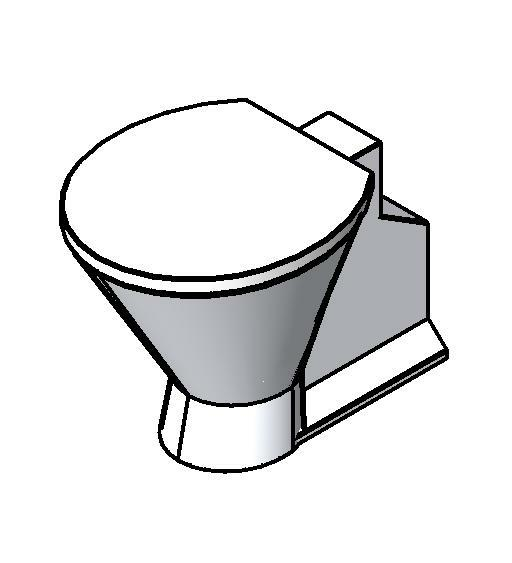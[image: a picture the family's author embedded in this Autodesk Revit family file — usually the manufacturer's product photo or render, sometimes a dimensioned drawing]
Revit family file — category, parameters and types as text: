
# Revit family: 23799-Deca_Torneira de Parede Cromado_Gama_1178-13
name_source: partatom
category: Plumbing Fixtures
units: mm (PartAtom-declared; Revit-internal decimal feet)

## family parameters
Cut with Voids When Loaded = No
Host = Face
Part Type = Normal
Room Calculation Point = No
Round Connector Dimension = Use Radius
Shared = No

## types (1)
- 1178.C13_CROMADO
    Acompanha o Produto = Bucha adaptadora de rosca
    Aprovado por = quattroD
    Atendimento ao Cliente = 0800 011 7073
    CWFU = 0
    Categoria = METAIS PARA BANHEIRO
    Composição Anel Vedação = -
    Composição Assento = -
    Composição Básica = Liga de Cobre (bronze e latão),Liga de Zinco(zamac),Plásticos de Engenharia,Elastômeros
    Composição Componente = -
    Consumo = -
    Cor Interna = -
    Cor Principal = Cromado
    Cor Secundária = -
    Cores Componente = -
    Criado por = quattroD
    Código Pai = 1178.C13
    Default Elevation = 1.1 m
    Description = TORNEIRA P/ LAVATORIO PAREDE DN15/20 GAMA - CROMADO
    Diâmetro Ponto de Esgoto = 0 m
    Diâmetro Água Fria = 0.02 m
    Informações Complementares = -
    Itens de Instalação = -
    Linha = Gama
    Manufacturer = Deca
    Material = Deca_Cromado
    Model = 1178.C13
    Norma = NBR 10281
    Peso Líquido (Kg) = 0.45
    Pressão mín. Aquec. Acúmulo = -
    Pressão mín. Aquec. Passagem = -
    Raio Ponto de Esgoto = 0 m
    Raio Água Fria = 0.01 m
    Saída de Esgoto = -
    Segmento = -
    Tipo de dispositivo economizador = RESTRITOR DECA COMFORT
    Tipo de mecanismo utilizado = MVC  - 1/4 de volta
    Tipo de rosca de entrada = BSP NBR 8133
    Tipo de rosca de saída = -
    URL = www.deca.com.br
    Vazão na Pressão máx. (L/min) = 6
    Vazão na Pressão mín. (L/min) = 4
    WFU = 0

## geometry (parser evidence)
native form markers: Sweep x1
no freeform markers — native parametric forms only
